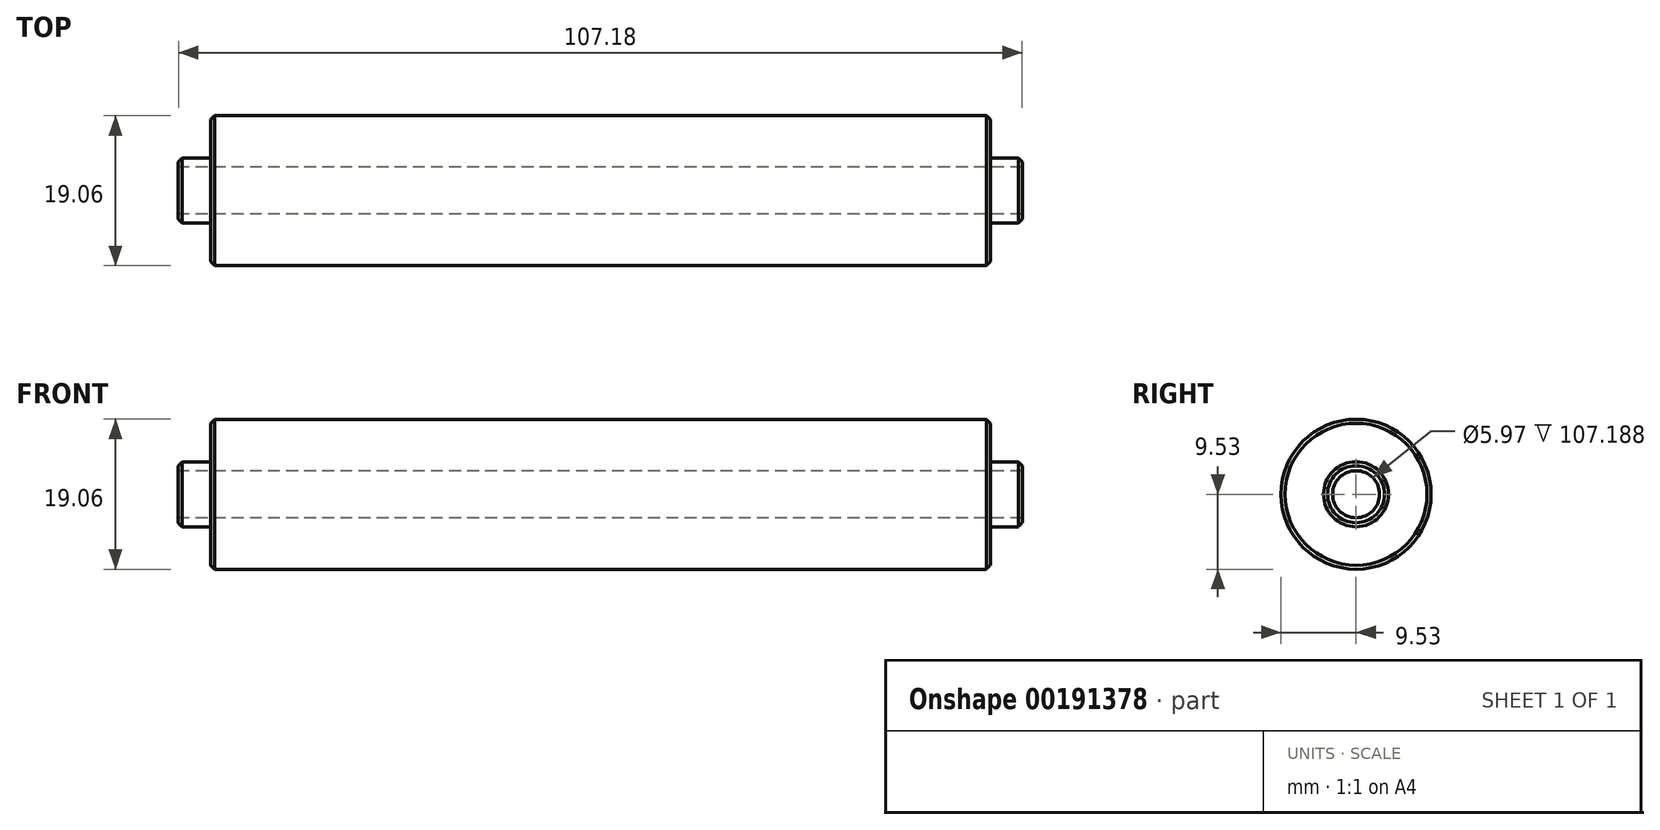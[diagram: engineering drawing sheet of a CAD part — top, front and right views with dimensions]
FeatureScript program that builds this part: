
annotation { "Feature Type Name" : "Feature", "Feature Type Description" : "" }
export const myFeature = defineFeature(function(context is Context, id is Id, definition is map)
    precondition{}
    {
        {
            var Q0;
            Q0=qCreatedBy(makeId("Right.planeOp"),FACE);
            var sketch = newSketch(context, id + "F0", { "sketchPlane" : qUnion([Q0])});
            skCircle(sketch, "E0", {"center": v(609.6, 0) * mm, "radius": 9.53 * mm});
            skSolve(sketch);
        }
        {
            var Q0;
            Q0=makeQuery(id+"F0.imprint","IMPRINT",FACE,{"disambiguationData":[TD([[makeQuery(id+"F0.imprint","IMPRINT",EDGE,{"derivedFrom":sQuery(id+"F0.wireOp",EDGE,"E0")}),1.0]])]});
            extrude(context, id + "F6", {"entities" : qUnion([Q0]), "depth" : 99.06 * mm});
        }
        {
            var Q0;
            Q0=makeQuery(id+"F6.opExtrude","CAP_FACE",FACE,{"disambiguationData":[OSD([sQuery(id+"F0.wireOp",EDGE,"E0")])],"isStart":false});
            var sketch = newSketch(context, id + "F7", { "sketchPlane" : qUnion([Q0])});
            skCircle(sketch, "E1", {"center": v(609.6, 0) * mm, "radius": 4.13 * mm});
            skSolve(sketch);
        }
        {
            var Q0;
            Q0=makeQuery(id+"F7.imprint","IMPRINT",FACE,{"disambiguationData":[TD([[makeQuery(id+"F7.imprint","IMPRINT",EDGE,{"derivedFrom":sQuery(id+"F7.wireOp",EDGE,"E1")}),1.0]])]});
            extrude(context, id + "F1", {"entities" : qUnion([Q0]), "operationType" : NewBodyOperationType.ADD, "depth" : 4.06 * mm});
        }
        {
            var Q0;
            Q0=makeQuery(id+"F1.opExtrude","CAP_FACE",FACE,{"disambiguationData":[OSD([sQuery(id+"F7.wireOp",EDGE,"E1")])],"isStart":false});
            var sketch = newSketch(context, id + "F2", { "sketchPlane" : qUnion([Q0])});
            skSolve(sketch);
        }
        {
            var Q0;
            Q0=makeQuery(id+"F6.opExtrude","CAP_FACE",FACE,{"disambiguationData":[OSD([sQuery(id+"F0.wireOp",EDGE,"E0")])],"isStart":true});
            var sketch = newSketch(context, id + "F3", { "sketchPlane" : qUnion([Q0])});
            skCircle(sketch, "E2", {"center": v(-609.6, 0) * mm, "radius": 4.13 * mm});
            skSolve(sketch);
        }
        {
            var Q0;
            Q0=makeQuery(id+"F3.imprint","IMPRINT",FACE,{"disambiguationData":[TD([[makeQuery(id+"F3.imprint","IMPRINT",EDGE,{"derivedFrom":sQuery(id+"F3.wireOp",EDGE,"E2")}),1.0]])]});
            extrude(context, id + "F8", {"entities" : qUnion([Q0]), "operationType" : NewBodyOperationType.ADD, "depth" : 4.06 * mm});
        }
        {
            var Q0;
            Q0=makeQuery(id+"F8.opExtrude","CAP_FACE",FACE,{"disambiguationData":[OSD([sQuery(id+"F3.wireOp",EDGE,"E2")])],"isStart":false});
            var sketch = newSketch(context, id + "F4", { "sketchPlane" : qUnion([Q0])});
            skCircle(sketch, "E3", {"center": v(-609.6, 0) * mm, "radius": 2.98 * mm});
            skSolve(sketch);
        }
        {
            var Q0;
            Q0=makeQuery(id+"F4.imprint","IMPRINT",FACE,{"disambiguationData":[TD([[makeQuery(id+"F4.imprint","IMPRINT",EDGE,{"derivedFrom":sQuery(id+"F4.wireOp",EDGE,"E3")}),1.0]])]});
            extrude(context, id + "F9", {"entities" : qUnion([Q0]), "operationType" : NewBodyOperationType.REMOVE, "endBound" : BoundingType.THROUGH_ALL, "oppositeDirection" : true, "depth" : 107.95 * mm});
        }
        {
            var Q0;
            Q0=makeQuery(id+"F6.opExtrude","CAP_EDGE",EDGE,{"disambiguationData":[OSD([sQuery(id+"F0.wireOp",EDGE,"E0")])],"isStart":false});
            var Q1;
            Q1=makeQuery(id+"F6.opExtrude","CAP_EDGE",EDGE,{"disambiguationData":[OSD([sQuery(id+"F0.wireOp",EDGE,"E0")])],"isStart":true});
            var Q2;
            Q2=makeQuery(id+"F8.opExtrude","CAP_EDGE",EDGE,{"disambiguationData":[OSD([sQuery(id+"F3.wireOp",EDGE,"E2")])],"isStart":false});
            var Q3;
            Q3=makeQuery(id+"F1.opExtrude","CAP_EDGE",EDGE,{"disambiguationData":[OSD([sQuery(id+"F7.wireOp",EDGE,"E1")])],"isStart":false});
            chamfer(context, id + "F5", {"entities" : qUnion([Q0, Q1, Q2, Q3]), "width" : 0.5 * mm, "tangentPropagation" : true});
        }
    });
